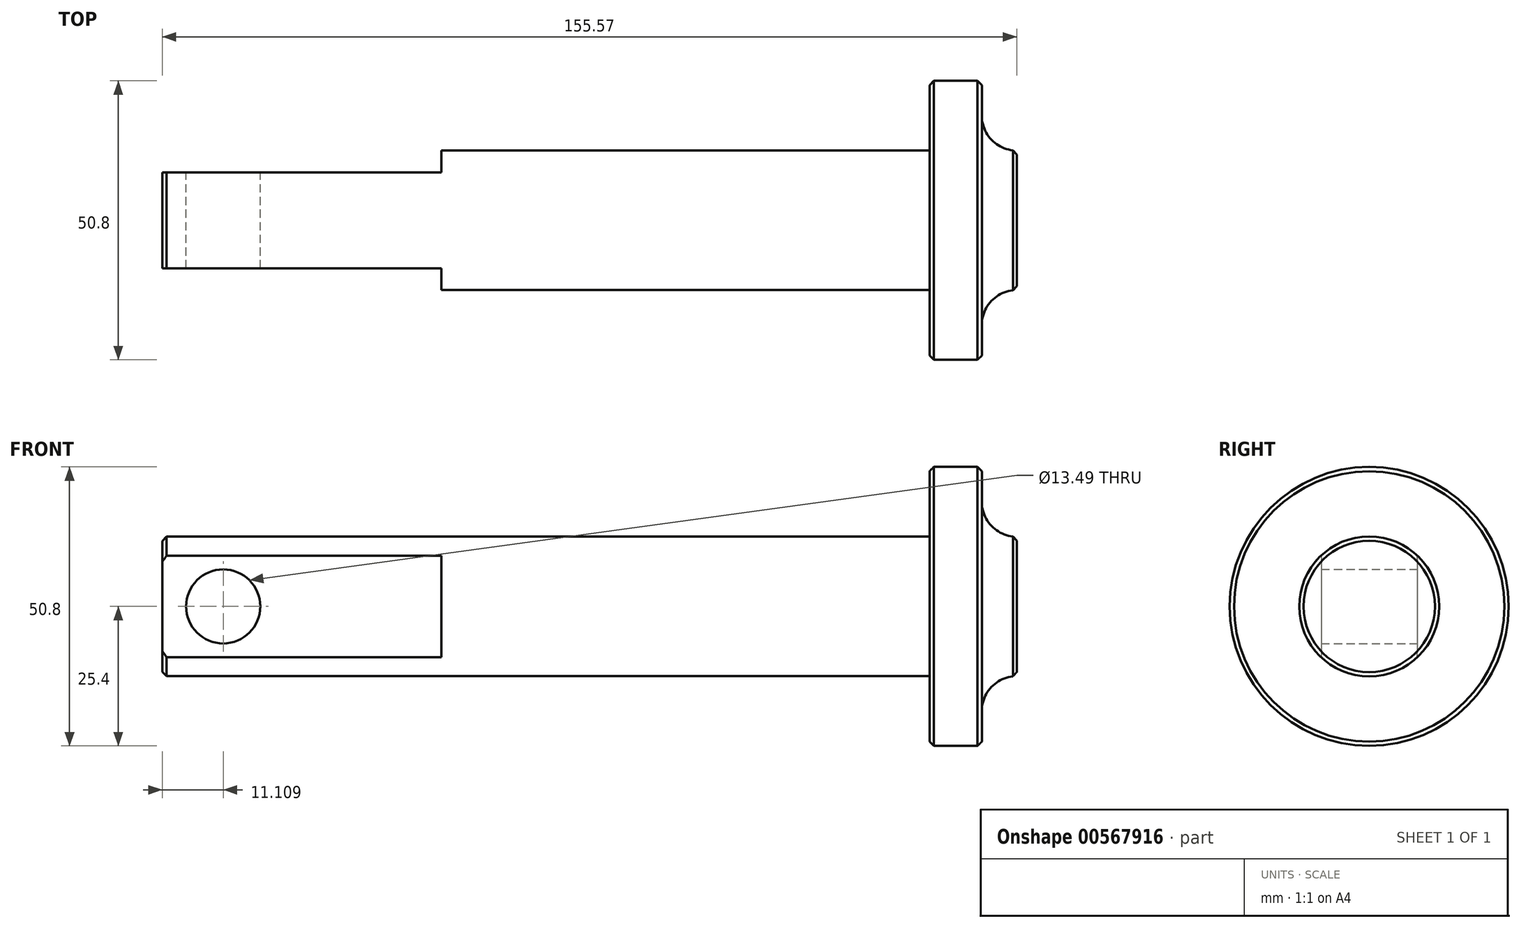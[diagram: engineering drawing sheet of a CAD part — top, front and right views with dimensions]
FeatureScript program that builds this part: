
annotation { "Feature Type Name" : "Feature", "Feature Type Description" : "" }
export const myFeature = defineFeature(function(context is Context, id is Id, definition is map)
    precondition{}
    {
        {
            var Q0;
            Q0=qCreatedBy(makeId("Front.planeOp"),FACE);
            var sketch = newSketch(context, id + "F0", { "sketchPlane" : qUnion([Q0])});
            skLineSegment(sketch, "E0", {"start": v(162.24, 0) * mm, "end": v(162.24, 12.7) * mm});
            skLineSegment(sketch, "E1", {"start": v(162.24, 12.7) * mm, "end": v(155.9, 12.7) * mm});
            skLineSegment(sketch, "E2", {"start": v(155.9, 12.7) * mm, "end": v(155.9, 25.4) * mm});
            skLineSegment(sketch, "E3", {"start": v(155.9, 25.4) * mm, "end": v(146.37, 25.4) * mm});
            skLineSegment(sketch, "E4", {"start": v(146.37, 25.4) * mm, "end": v(146.37, 12.7) * mm});
            skLineSegment(sketch, "E5", {"start": v(146.37, 12.7) * mm, "end": v(6.67, 12.7) * mm});
            skLineSegment(sketch, "E6", {"start": v(6.67, 12.7) * mm, "end": v(6.67, 0) * mm});
            skLineSegment(sketch, "E7", {"start": v(162.24, 0) * mm, "end": v(6.67, 0) * mm});
            skSolve(sketch);
        }
        {
            var Q0;
            Q0=makeQuery(id+"F0.imprint","IMPRINT",FACE,{"disambiguationData":[TD([[makeQuery(id+"F0.imprint","IMPRINT",EDGE,{"derivedFrom":sQuery(id+"F0.wireOp",EDGE,"E0")}),1.0]])]});
            var Q1;
            Q1=sQuery(id+"F0.wireOp",EDGE,"E7");
            revolve(context, id + "F1", {"entities" : qUnion([Q0]), "axis" : qUnion([Q1]), "revolveType" : RevolveType.FULL});
        }
        {
            var Q0;
            Q0=makeQuery(id+"F1.opRevolve","SWEPT_EDGE",EDGE,{"disambiguationData":[OSD([sQuery(id+"F0.wireOp",EDGE,"E1"),sQuery(id+"F0.wireOp",EDGE,"E2")])]});
            fillet(context, id + "F2", {"entities" : qUnion([Q0]), "radius" : 6.35 * mm, "tangentPropagation" : true, "allowEdgeOverflow" : false});
        }
        {
            var Q0;
            Q0=makeQuery(id+"F1.opRevolve","SWEPT_FACE",FACE,{"disambiguationData":[OSD([sQuery(id+"F0.wireOp",EDGE,"E6")])]});
            var sketch = newSketch(context, id + "F3", { "sketchPlane" : qUnion([Q0])});
            skLineSegment(sketch, "E8", {"start": v(0, 12.7) * mm, "end": v(0, -12.7) * mm});
            skLineSegment(sketch, "E9.0", {"start": v(-8.73, 12.7) * mm, "end": v(-8.73, -12.7) * mm});
            skLineSegment(sketch, "E10.0", {"start": v(8.73, 12.7) * mm, "end": v(8.73, -12.7) * mm});
            skSolve(sketch);
        }
        {
            var Q0;
            {var subQ0=sQuery(id+"F3.wireOp",EDGE,"E9.0");var subQ1=makeQuery(id+"F1.opRevolve","SWEPT_EDGE",EDGE,{"disambiguationData":[OSD([sQuery(id+"F0.wireOp",EDGE,"E5"),sQuery(id+"F0.wireOp",EDGE,"E6")])]});var subQ2=makeQuery(id+"F3.imprint","INTERSECT",VERTEX,{"disambiguationData":[OD(0.0)],"derivedFrom":[subQ1,subQ0]});Q0=makeQuery(id+"F3.imprint","IMPRINT",FACE,{"disambiguationData":[TD([[makeQuery(id+"F3.imprint","IMPRINT",EDGE,{"disambiguationData":[TD([[subQ2,-1.0]])],"derivedFrom":subQ0}),-1.0]])]});}
            var Q1;
            {var subQ0=sQuery(id+"F3.wireOp",EDGE,"E10.0");var subQ1=makeQuery(id+"F1.opRevolve","SWEPT_EDGE",EDGE,{"disambiguationData":[OSD([sQuery(id+"F0.wireOp",EDGE,"E5"),sQuery(id+"F0.wireOp",EDGE,"E6")])]});var subQ2=makeQuery(id+"F3.imprint","INTERSECT",VERTEX,{"disambiguationData":[OD(0.0)],"derivedFrom":[subQ1,subQ0]});Q1=makeQuery(id+"F3.imprint","IMPRINT",FACE,{"disambiguationData":[TD([[makeQuery(id+"F3.imprint","IMPRINT",EDGE,{"disambiguationData":[TD([[subQ2,-1.0]])],"derivedFrom":subQ0}),1.0]])]});}
            extrude(context, id + "F4", {"entities" : qUnion([Q0, Q1]), "operationType" : NewBodyOperationType.REMOVE, "oppositeDirection" : true, "depth" : 50.8 * mm});
        }
        {
            var Q0;
            Q0=makeQuery(id+"F4.boolean.opBoolean","COPY",FACE,{"derivedFrom":makeQuery(id+"F4.opExtrude","SWEPT_FACE",FACE,{"disambiguationData":[OSD([sQuery(id+"F3.wireOp",EDGE,"E10.0")])]})});
            var sketch = newSketch(context, id + "F5", { "sketchPlane" : qUnion([Q0])});
            skLineSegment(sketch, "E11", {"start": v(57.47, 9.22) * mm, "end": v(57.47, -9.22) * mm});
            skLineSegment(sketch, "E12.0", {"start": v(17.78, 9.22) * mm, "end": v(17.78, -9.22) * mm});
            skLineSegment(sketch, "E13.0", {"start": v(0.32, 15.57) * mm, "end": v(0.32, -15.57) * mm});
            skLineSegment(sketch, "E13.1", {"start": v(63.82, 15.57) * mm, "end": v(0.32, 15.57) * mm});
            skLineSegment(sketch, "E13.2", {"start": v(63.82, -15.57) * mm, "end": v(63.82, 15.57) * mm});
            skLineSegment(sketch, "E13.3", {"start": v(0.32, -15.57) * mm, "end": v(63.82, -15.57) * mm});
            skPoint(sketch, "E14", {"position": v(17.78, 0) * mm});
            skSolve(sketch);
        }
        {
            var Q0;
            Q0=sQuery(id+"F5.wireOp",VERTEX,"E14");
            var Q1;
            Q1=makeQuery(id+"F1.opRevolve","SWEPT_BODY",BODY,{"disambiguationData":[OSD([sQuery(id+"F0.wireOp",EDGE,"E0"),sQuery(id+"F0.wireOp",EDGE,"E1"),sQuery(id+"F0.wireOp",EDGE,"E2"),sQuery(id+"F0.wireOp",EDGE,"E3"),sQuery(id+"F0.wireOp",EDGE,"E4"),sQuery(id+"F0.wireOp",EDGE,"E5"),sQuery(id+"F0.wireOp",EDGE,"E6"),sQuery(id+"F0.wireOp",EDGE,"E7")])]});
            hole(context, id + "F6", {"style" : HoleStyle.SIMPLE, "endStyle" : HoleEndStyle.THROUGH, "holeDiameter" : 13.5 * mm, "locations" : qUnion([Q0]), "scope" : qUnion([Q1]), "isTappedThrough" : true});
        }
        {
            var Q0;
            Q0=makeQuery(id+"F4.boolean.opBoolean","SPLIT",EDGE,{"disambiguationData":[OD(0.0)],"derivedFrom":makeQuery(id+"F1.opRevolve","SWEPT_EDGE",EDGE,{"disambiguationData":[OSD([sQuery(id+"F0.wireOp",EDGE,"E5"),sQuery(id+"F0.wireOp",EDGE,"E6")])]})});
            var Q1;
            Q1=makeQuery(id+"F4.boolean.opBoolean","COPY",EDGE,{"derivedFrom":makeQuery(id+"F4.opExtrude","CAP_EDGE",EDGE,{"disambiguationData":[OSD([sQuery(id+"F3.wireOp",EDGE,"E10.0")])],"isStart":true})});
            var Q2;
            Q2=makeQuery(id+"F4.boolean.opBoolean","SPLIT",EDGE,{"disambiguationData":[OD(1.0)],"derivedFrom":makeQuery(id+"F1.opRevolve","SWEPT_EDGE",EDGE,{"disambiguationData":[OSD([sQuery(id+"F0.wireOp",EDGE,"E5"),sQuery(id+"F0.wireOp",EDGE,"E6")])]})});
            var Q3;
            Q3=makeQuery(id+"F4.boolean.opBoolean","COPY",EDGE,{"derivedFrom":makeQuery(id+"F4.opExtrude","CAP_EDGE",EDGE,{"disambiguationData":[OSD([sQuery(id+"F3.wireOp",EDGE,"E9.0")])],"isStart":true})});
            var Q4;
            {var subQ0=sQuery(id+"F3.wireOp",EDGE,"E10.0");var subQ1=sQuery(id+"F0.wireOp",EDGE,"E6");var subQ2=sQuery(id+"F0.wireOp",EDGE,"E5");Q4=makeQuery(id+"F4.boolean.opBoolean","COPY",EDGE,{"derivedFrom":makeQuery(id+"F4.opExtrude","SWEPT_EDGE",EDGE,{"disambiguationData":[OSD([subQ2,subQ1,subQ0]),TDD([makeQuery(id+"F3.imprint","INTERSECT",VERTEX,{"disambiguationData":[OD(0.0)],"derivedFrom":[makeQuery(id+"F1.opRevolve","SWEPT_EDGE",EDGE,{"disambiguationData":[OSD([subQ2,subQ1])]}),subQ0]})])]})});}
            var Q5;
            {var subQ0=sQuery(id+"F3.wireOp",EDGE,"E10.0");var subQ1=sQuery(id+"F0.wireOp",EDGE,"E6");var subQ2=sQuery(id+"F0.wireOp",EDGE,"E5");Q5=makeQuery(id+"F4.boolean.opBoolean","COPY",EDGE,{"derivedFrom":makeQuery(id+"F4.opExtrude","SWEPT_EDGE",EDGE,{"disambiguationData":[OSD([subQ2,subQ1,subQ0]),TDD([makeQuery(id+"F3.imprint","INTERSECT",VERTEX,{"disambiguationData":[OD(1.0)],"derivedFrom":[makeQuery(id+"F1.opRevolve","SWEPT_EDGE",EDGE,{"disambiguationData":[OSD([subQ2,subQ1])]}),subQ0]})])]})});}
            var Q6;
            Q6=makeQuery(id+"F6.hole-0.boolean.opBoolean","COPY",EDGE,{"derivedFrom":makeQuery(id+"F6.hole-0.opRevolve","SWEPT_EDGE",EDGE,{"disambiguationData":[OSD([sQuery(id+"F6.hole-0.sketch.wireOp",EDGE,"core_line_2"),sQuery(id+"F6.hole-0.sketch.wireOp",EDGE,"core_line_3")])]})});
            var Q7;
            {var subQ0=sQuery(id+"F3.wireOp",EDGE,"E9.0");var subQ1=sQuery(id+"F0.wireOp",EDGE,"E6");var subQ2=sQuery(id+"F0.wireOp",EDGE,"E5");Q7=makeQuery(id+"F4.boolean.opBoolean","COPY",EDGE,{"derivedFrom":makeQuery(id+"F4.opExtrude","SWEPT_EDGE",EDGE,{"disambiguationData":[OSD([subQ2,subQ1,subQ0]),TDD([makeQuery(id+"F3.imprint","INTERSECT",VERTEX,{"disambiguationData":[OD(0.0)],"derivedFrom":[makeQuery(id+"F1.opRevolve","SWEPT_EDGE",EDGE,{"disambiguationData":[OSD([subQ2,subQ1])]}),subQ0]})])]})});}
            var Q8;
            Q8=makeQuery(id+"F6.hole-0.boolean.opBoolean","INTERSECT",EDGE,{"derivedFrom":[makeQuery(id+"F4.boolean.opBoolean","COPY",FACE,{"derivedFrom":makeQuery(id+"F4.opExtrude","SWEPT_FACE",FACE,{"disambiguationData":[OSD([sQuery(id+"F3.wireOp",EDGE,"E9.0")])]})}),makeQuery(id+"F6.hole-0.opRevolve","SWEPT_FACE",FACE,{"disambiguationData":[OSD([sQuery(id+"F6.hole-0.sketch.wireOp",EDGE,"core_line_2")])]})]});
            var Q9;
            {var subQ0=sQuery(id+"F3.wireOp",EDGE,"E9.0");var subQ1=sQuery(id+"F0.wireOp",EDGE,"E6");var subQ2=sQuery(id+"F0.wireOp",EDGE,"E5");Q9=makeQuery(id+"F4.boolean.opBoolean","COPY",EDGE,{"derivedFrom":makeQuery(id+"F4.opExtrude","SWEPT_EDGE",EDGE,{"disambiguationData":[OSD([subQ2,subQ1,subQ0]),TDD([makeQuery(id+"F3.imprint","INTERSECT",VERTEX,{"disambiguationData":[OD(1.0)],"derivedFrom":[makeQuery(id+"F1.opRevolve","SWEPT_EDGE",EDGE,{"disambiguationData":[OSD([subQ2,subQ1])]}),subQ0]})])]})});}
            var Q10;
            Q10=makeQuery(id+"F1.opRevolve","SWEPT_EDGE",EDGE,{"disambiguationData":[OSD([sQuery(id+"F0.wireOp",EDGE,"E3"),sQuery(id+"F0.wireOp",EDGE,"E4")])]});
            var Q11;
            Q11=makeQuery(id+"F1.opRevolve","SWEPT_EDGE",EDGE,{"disambiguationData":[OSD([sQuery(id+"F0.wireOp",EDGE,"E2"),sQuery(id+"F0.wireOp",EDGE,"E3")])]});
            var Q12;
            Q12=makeQuery(id+"F2.opFillet","BLEND_EDGE",EDGE,{"blendedFrom":[makeQuery(id+"F1.opRevolve","SWEPT_EDGE",EDGE,{"disambiguationData":[OSD([sQuery(id+"F0.wireOp",EDGE,"E1"),sQuery(id+"F0.wireOp",EDGE,"E2")])]}),makeQuery(id+"F1.opRevolve","SWEPT_FACE",FACE,{"disambiguationData":[OSD([sQuery(id+"F0.wireOp",EDGE,"E0")])]})],"blendedInto":[makeQuery(id+"F1.opRevolve","SWEPT_FACE",FACE,{"disambiguationData":[OSD([sQuery(id+"F0.wireOp",EDGE,"E0")])]})]});
            chamfer(context, id + "F7", {"entities" : qUnion([Q0, Q1, Q2, Q3, Q4, Q5, Q6, Q7, Q8, Q9, Q10, Q11, Q12]), "width" : 0.79 * mm, "tangentPropagation" : true});
        }
    });
